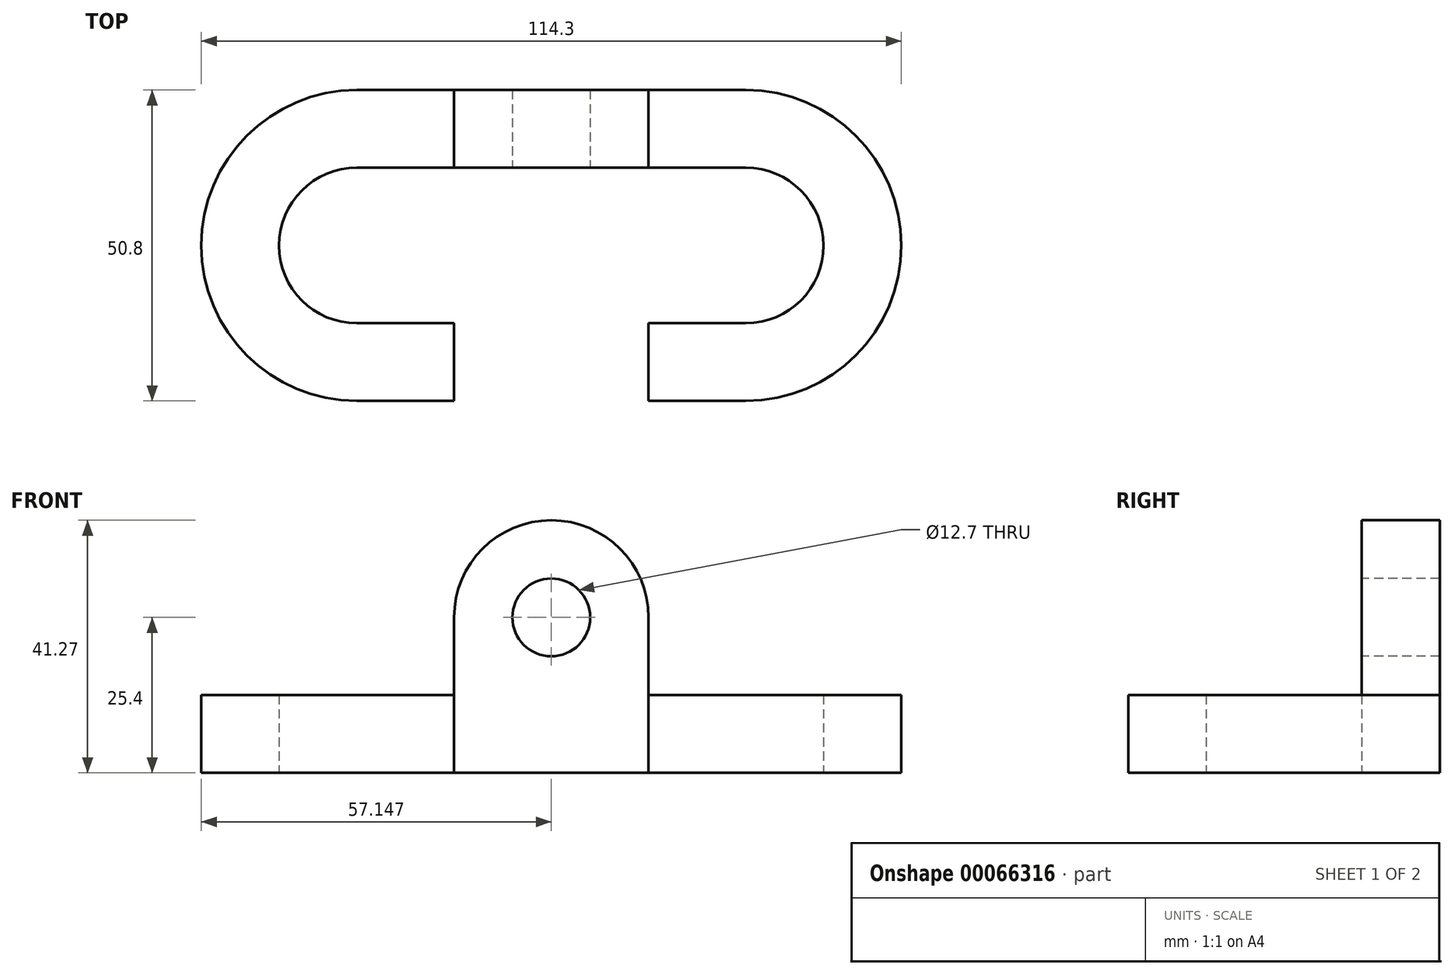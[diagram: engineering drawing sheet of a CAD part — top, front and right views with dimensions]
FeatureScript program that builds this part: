
annotation { "Feature Type Name" : "Feature", "Feature Type Description" : "" }
export const myFeature = defineFeature(function(context is Context, id is Id, definition is map)
    precondition{}
    {
        {
            var Q0;
            Q0=qCreatedBy(makeId("Top.planeOp"),FACE);
            var sketch = newSketch(context, id + "F0", { "sketchPlane" : qUnion([Q0])});
            skPoint(sketch, "E0", {"position": v(-48.35, 0) * mm});
            skPoint(sketch, "E1", {"position": v(15.15, 0) * mm});
            skPoint(sketch, "E2", {"position": v(-48.35, 6.35) * mm});
            skPoint(sketch, "E3", {"position": v(12.25, -6.72) * mm});
            skPoint(sketch, "E4", {"position": v(15.15, -6.35) * mm});
            skLineSegment(sketch, "E5.bottom", {"start": v(-48.35, 6.35) * mm, "end": v(15.15, 6.35) * mm});
            skLineSegment(sketch, "E5.top", {"start": v(-48.35, -6.35) * mm, "end": v(15.15, -6.35) * mm});
            skArc(sketch, "E6", {"start": v(15.15, -31.75) * mm, "mid": v(27.85, -19.05) * mm, "end": v(15.15, -6.35) * mm});
            skPoint(sketch, "E7", {"position": v(-0.73, -31.75) * mm});
            skPoint(sketch, "E8", {"position": v(15.15, -44.45) * mm});
            skLineSegment(sketch, "E9.bottom", {"start": v(15.15, -44.45) * mm, "end": v(-0.73, -44.45) * mm});
            skLineSegment(sketch, "E9.top", {"start": v(15.15, -31.75) * mm, "end": v(-0.73, -31.75) * mm});
            skLineSegment(sketch, "E9.right", {"start": v(-0.73, -44.45) * mm, "end": v(-0.73, -31.75) * mm});
            skArc(sketch, "E10", {"start": v(15.15, -44.45) * mm, "mid": v(40.55, -19.05) * mm, "end": v(15.15, 6.35) * mm});
            skArc(sketch, "E11", {"start": v(-48.35, -6.35) * mm, "mid": v(-61.05, -19.05) * mm, "end": v(-48.35, -31.75) * mm});
            skLineSegment(sketch, "E12.bottom", {"start": v(-48.35, -31.75) * mm, "end": v(-32.48, -31.75) * mm});
            skLineSegment(sketch, "E12.top", {"start": v(-48.35, -44.45) * mm, "end": v(-32.48, -44.45) * mm});
            skLineSegment(sketch, "E12.right", {"start": v(-32.48, -31.75) * mm, "end": v(-32.48, -44.45) * mm});
            skArc(sketch, "E13", {"start": v(-48.35, 6.35) * mm, "mid": v(-73.75, -19.05) * mm, "end": v(-48.35, -44.45) * mm});
            skSolve(sketch);
        }
        {
            var Q0;
            Q0 = qSketchRegion(id + "F0", true);
            extrude(context, id + "F1", {"entities" : qUnion([Q0]), "depth" : 12.7 * mm});
        }
        {
            var Q0;
            Q0=makeQuery(id+"F1.opExtrude","SWEPT_FACE",FACE,{"disambiguationData":[OSD([sQuery(id+"F0.wireOp",EDGE,"E5.top")])]});
            var sketch = newSketch(context, id + "F2", { "sketchPlane" : qUnion([Q0])});
            skPoint(sketch, "E14", {"position": v(-16.6, 12.7) * mm});
            skPoint(sketch, "E15", {"position": v(-16.6, 0) * mm});
            skPoint(sketch, "E16", {"position": v(-16.6, 25.4) * mm});
            skCircle(sketch, "E17", {"center": v(-16.6, 25.4) * mm, "radius": 6.35 * mm});
            skPoint(sketch, "E18", {"position": v(-32.48, 25.4) * mm});
            skPoint(sketch, "E19", {"position": v(-0.73, 25.4) * mm});
            skArc(sketch, "E20", {"start": v(-0.73, 25.4) * mm, "mid": v(-16.6, 41.28) * mm, "end": v(-32.48, 25.4) * mm});
            skLineSegment(sketch, "E21", {"start": v(-0.96, 24.54) * mm, "end": v(-2.53, 22.25) * mm});
            skLineSegment(sketch, "E22", {"start": v(-0.73, 25.4) * mm, "end": v(-0.73, 12.7) * mm});
            skLineSegment(sketch, "E23", {"start": v(-32.48, 25.4) * mm, "end": v(-32.48, 12.7) * mm});
            skSolve(sketch);
        }
        {
            var Q0;
            Q0=makeQuery(id+"F2.imprint","IMPRINT",FACE,{"disambiguationData":[TD([[makeQuery(id+"F2.imprint","IMPRINT",EDGE,{"derivedFrom":sQuery(id+"F2.wireOp",EDGE,"E17")}),-1.0]])]});
            extrude(context, id + "F3", {"entities" : qUnion([Q0]), "operationType" : NewBodyOperationType.ADD, "oppositeDirection" : true, "depth" : 12.7 * mm});
        }
    });
